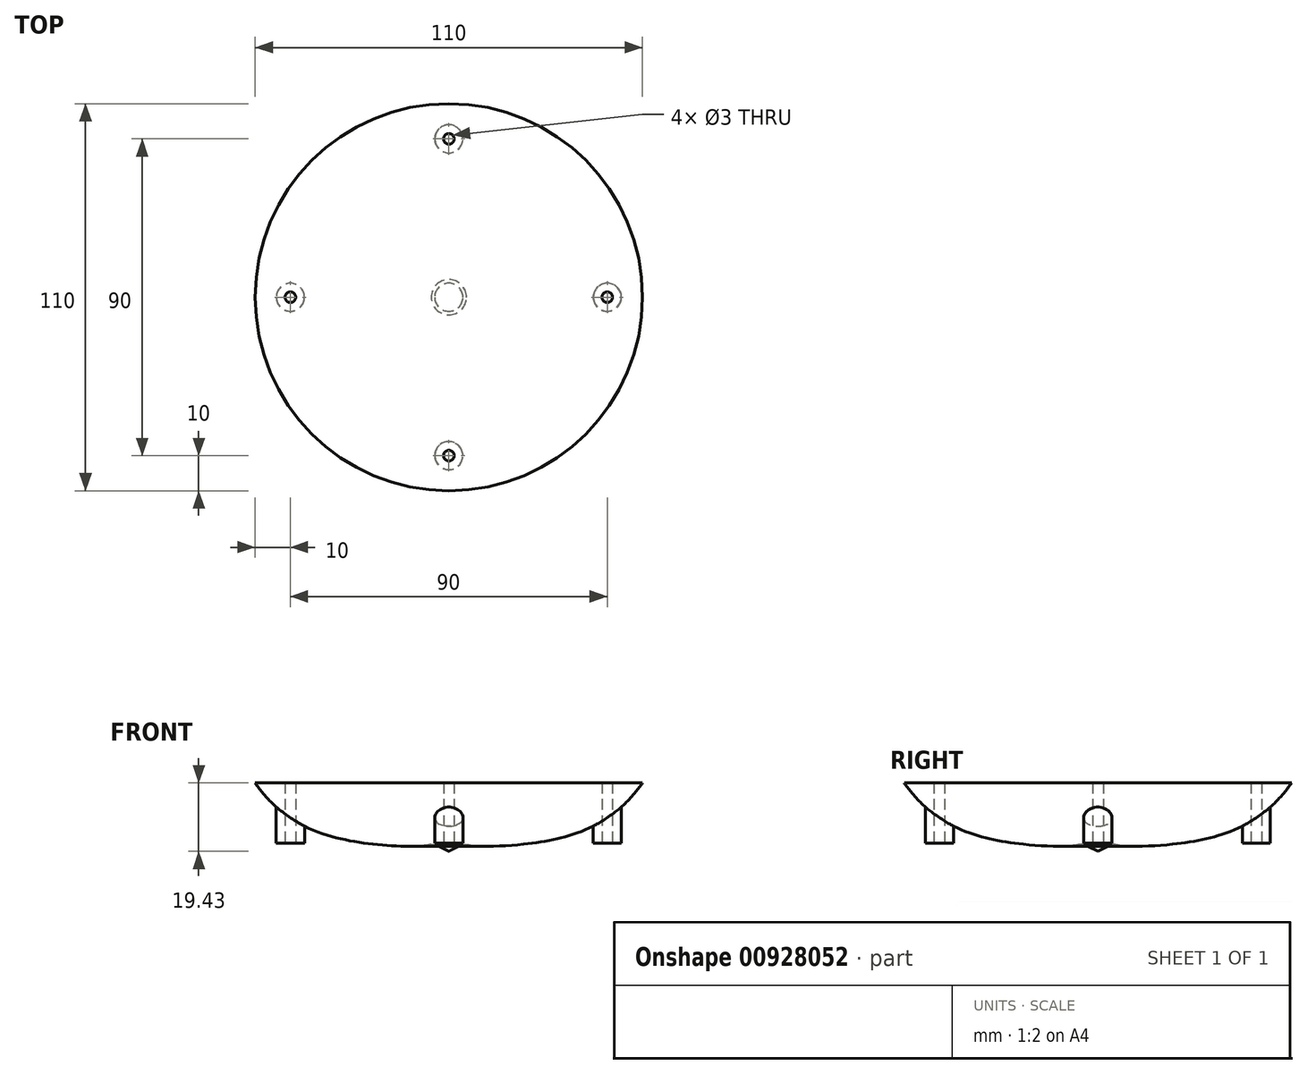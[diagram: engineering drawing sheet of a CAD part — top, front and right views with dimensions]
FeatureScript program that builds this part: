
annotation { "Feature Type Name" : "Feature", "Feature Type Description" : "" }
export const myFeature = defineFeature(function(context is Context, id is Id, definition is map)
    precondition{}
    {
        {
            var Q0;
            Q0=qCreatedBy(makeId("Front.planeOp"),FACE);
            var sketch = newSketch(context, id + "F0", { "sketchPlane" : qUnion([Q0])});
            skPoint(sketch, "E0", {"position": v(5, 2.5) * mm});
            skPoint(sketch, "E1", {"position": v(6, 2.28) * mm});
            skPoint(sketch, "E2", {"position": v(10, 1.95) * mm});
            skPoint(sketch, "E3", {"position": v(12, 1.95) * mm});
            skPoint(sketch, "E4", {"position": v(14, 2) * mm});
            skPoint(sketch, "E5", {"position": v(16, 2.1) * mm});
            skPoint(sketch, "E6", {"position": v(18, 2.22) * mm});
            skPoint(sketch, "E7", {"position": v(20, 2.4) * mm});
            skPoint(sketch, "E8", {"position": v(23, 2.72) * mm});
            skPoint(sketch, "E9", {"position": v(24, 2.85) * mm});
            skPoint(sketch, "E10", {"position": v(25, 3) * mm});
            skPoint(sketch, "E11", {"position": v(8, 2.04) * mm});
            skPoint(sketch, "E12", {"position": v(9, 1.98) * mm});
            skPoint(sketch, "E13", {"position": v(7, 2.13) * mm});
            skPoint(sketch, "E14", {"position": v(11, 1.94) * mm});
            skPoint(sketch, "E15", {"position": v(13, 1.97) * mm});
            skPoint(sketch, "E16", {"position": v(15, 2.04) * mm});
            skPoint(sketch, "E17", {"position": v(17, 2.15) * mm});
            skPoint(sketch, "E18", {"position": v(19, 2.3) * mm});
            skPoint(sketch, "E19", {"position": v(21, 2.5) * mm});
            skPoint(sketch, "E20", {"position": v(22, 2.6) * mm});
            skPoint(sketch, "E21", {"position": v(26, 3.15) * mm});
            skPoint(sketch, "E22", {"position": v(27, 3.31) * mm});
            skPoint(sketch, "E23", {"position": v(28, 3.5) * mm});
            skPoint(sketch, "E24", {"position": v(29, 3.7) * mm});
            skPoint(sketch, "E25", {"position": v(30, 3.9) * mm});
            skPoint(sketch, "E26", {"position": v(31, 4.13) * mm});
            skPoint(sketch, "E27", {"position": v(32, 4.37) * mm});
            skPoint(sketch, "E28", {"position": v(33, 4.64) * mm});
            skPoint(sketch, "E29", {"position": v(34, 4.92) * mm});
            skPoint(sketch, "E30", {"position": v(35, 5.23) * mm});
            skPoint(sketch, "E31", {"position": v(36, 5.56) * mm});
            skPoint(sketch, "E32", {"position": v(37, 5.92) * mm});
            skPoint(sketch, "E33", {"position": v(38, 6.3) * mm});
            skPoint(sketch, "E34", {"position": v(39, 6.71) * mm});
            skPoint(sketch, "E35", {"position": v(40, 7.16) * mm});
            skPoint(sketch, "E36", {"position": v(41, 7.64) * mm});
            skPoint(sketch, "E37", {"position": v(42, 8.15) * mm});
            skPoint(sketch, "E38", {"position": v(44, 9.31) * mm});
            skPoint(sketch, "E39", {"position": v(45, 9.95) * mm});
            skPoint(sketch, "E40", {"position": v(43, 8.71) * mm});
            skPoint(sketch, "E41", {"position": v(52, 16.11) * mm});
            skPoint(sketch, "E42", {"position": v(55, 19.93) * mm});
            skPoint(sketch, "E43", {"position": v(0, 0) * mm});
            skPoint(sketch, "E44", {"position": v(54, 18.56) * mm});
            skPoint(sketch, "E45", {"position": v(53, 17.29) * mm});
            skPoint(sketch, "E46", {"position": v(51, 15.02) * mm});
            skPoint(sketch, "E47", {"position": v(50, 14) * mm});
            skPoint(sketch, "E48", {"position": v(49, 13.07) * mm});
            skPoint(sketch, "E49", {"position": v(48, 12.2) * mm});
            skPoint(sketch, "E50", {"position": v(47, 11.4) * mm});
            skPoint(sketch, "E51", {"position": v(46, 10.65) * mm});
            skPoint(sketch, "E52", {"position": v(0, 2.5) * mm});
            skLineSegment(sketch, "E53", {"start": v(0, 2.5) * mm, "end": v(5, 2.5) * mm});
            skFitSpline(sketch, "E54", {"points": [v(5, 2.5) * mm, v(6, 2.28) * mm, v(7, 2.13) * mm, v(8, 2.04) * mm, v(9, 1.98) * mm, v(10, 1.95) * mm, v(11, 1.94) * mm, v(12, 1.95) * mm, v(13, 1.97) * mm, v(14, 2) * mm, v(15, 2.04) * mm, v(16, 2.1) * mm, v(17, 2.15) * mm, v(18, 2.22) * mm, v(19, 2.3) * mm, v(20, 2.4) * mm, v(21, 2.5) * mm, v(22, 2.6) * mm, v(23, 2.72) * mm, v(24, 2.85) * mm, v(25, 3) * mm, v(26, 3.15) * mm, v(27, 3.31) * mm, v(28, 3.5) * mm, v(29, 3.7) * mm, v(30, 3.9) * mm, v(31, 4.13) * mm, v(32, 4.37) * mm, v(33, 4.64) * mm, v(34, 4.92) * mm, v(35, 5.23) * mm, v(36, 5.56) * mm, v(37, 5.92) * mm, v(38, 6.3) * mm, v(39, 6.71) * mm, v(40, 7.16) * mm, v(41, 7.64) * mm, v(42, 8.15) * mm, v(43, 8.71) * mm, v(44, 9.31) * mm, v(45, 9.95) * mm, v(46, 10.65) * mm, v(47, 11.4) * mm, v(48, 12.2) * mm, v(49, 13.07) * mm, v(50, 14) * mm, v(51, 15.02) * mm, v(52, 16.11) * mm, v(53, 17.29) * mm, v(54, 18.56) * mm, v(55, 19.93) * mm], "startDerivative": vector(51.92, -12.2) * mm, "endDerivative": vector(40.18, 55.95) * mm});
            skPoint(sketch, "E55", {"position": v(0, 19.93) * mm});
            skLineSegment(sketch, "E56", {"start": v(0, 2.5) * mm, "end": v(0, 19.93) * mm});
            skLineSegment(sketch, "E57", {"start": v(0, 19.93) * mm, "end": v(55, 19.93) * mm});
            skLineSegment(sketch, "E58", {"start": v(0, -53.88) * mm, "end": v(0, 63.92) * mm, "construction": true});
            skSolve(sketch);
        }
        {
            var Q0;
            Q0=makeQuery(id+"F0.imprint","IMPRINT",FACE,{"disambiguationData":[TD([[makeQuery(id+"F0.imprint","IMPRINT",EDGE,{"derivedFrom":sQuery(id+"F0.wireOp",EDGE,"E53")}),1.0]])]});
            var Q1;
            Q1=sQuery(id+"F0.wireOp",EDGE,"E58");
            revolve(context, id + "F1", {"surfaceOperationType" : NewSurfaceOperationType.NEW, "entities" : qUnion([Q0]), "axis" : qUnion([Q1]), "revolveType" : RevolveType.FULL});
        }
        {
            var Q0;
            Q0=qCreatedBy(makeId("Top.planeOp"),FACE);
            cPlane(context, id + "F2", {"entities" : qUnion([Q0]), "cplaneType" : CPlaneType.OFFSET, "offset" : 2.8 * mm, "width" : 150 * mm, "height" : 150 * mm});
        }
        {
            var Q0;
            Q0=qCreatedBy(id+"F2.planeOp",FACE);
            var sketch = newSketch(context, id + "F3", { "sketchPlane" : qUnion([Q0])});
            skCircle(sketch, "E59", {"center": v(45, 0) * mm, "radius": 4 * mm});
            skCircle(sketch, "E60.1.1", {"center": v(0, 45) * mm, "radius": 4 * mm});
            skCircle(sketch, "E60.2.1", {"center": v(-45, 0) * mm, "radius": 4 * mm});
            skCircle(sketch, "E60.3.1", {"center": v(0, -45) * mm, "radius": 4 * mm});
            skPoint(sketch, "E60.center", {"position": v(0, 0) * mm});
            skSolve(sketch);
        }
        {
            var Q0;
            Q0=makeQuery(id+"F3.imprint","IMPRINT",FACE,{"disambiguationData":[TD([[makeQuery(id+"F3.imprint","IMPRINT",EDGE,{"derivedFrom":sQuery(id+"F3.wireOp",EDGE,"E60.3.1")}),1.0]])]});
            var Q1;
            Q1=makeQuery(id+"F3.imprint","IMPRINT",FACE,{"disambiguationData":[TD([[makeQuery(id+"F3.imprint","IMPRINT",EDGE,{"derivedFrom":sQuery(id+"F3.wireOp",EDGE,"E59")}),1.0]])]});
            var Q2;
            Q2=makeQuery(id+"F3.imprint","IMPRINT",FACE,{"disambiguationData":[TD([[makeQuery(id+"F3.imprint","IMPRINT",EDGE,{"derivedFrom":sQuery(id+"F3.wireOp",EDGE,"E60.1.1")}),1.0]])]});
            var Q3;
            Q3=makeQuery(id+"F3.imprint","IMPRINT",FACE,{"disambiguationData":[TD([[makeQuery(id+"F3.imprint","IMPRINT",EDGE,{"derivedFrom":sQuery(id+"F3.wireOp",EDGE,"E60.2.1")}),1.0]])]});
            extrude(context, id + "F4", {"entities" : qUnion([Q0, Q1, Q2, Q3]), "operationType" : NewBodyOperationType.ADD, "depth" : 12 * mm, "offsetDistance" : 25 * mm});
        }
        {
            var Q0;
            Q0=qCreatedBy(id+"F2.planeOp",FACE);
            var sketch = newSketch(context, id + "F5", { "sketchPlane" : qUnion([Q0])});
            skCircle(sketch, "E61", {"center": v(45, 0) * mm, "radius": 1.5 * mm});
            skCircle(sketch, "E62.1.0", {"center": v(0, 45) * mm, "radius": 1.5 * mm});
            skCircle(sketch, "E62.2.0", {"center": v(-45, 0) * mm, "radius": 1.5 * mm});
            skCircle(sketch, "E62.3.0", {"center": v(0, -45) * mm, "radius": 1.5 * mm});
            skPoint(sketch, "E62.center", {"position": v(0, 0) * mm});
            skSolve(sketch);
        }
        {
            var Q0;
            Q0=makeQuery(id+"F5.imprint","IMPRINT",FACE,{"disambiguationData":[TD([[makeQuery(id+"F5.imprint","IMPRINT",EDGE,{"derivedFrom":sQuery(id+"F5.wireOp",EDGE,"E61")}),1.0]])]});
            var Q1;
            Q1=makeQuery(id+"F5.imprint","IMPRINT",FACE,{"disambiguationData":[TD([[makeQuery(id+"F5.imprint","IMPRINT",EDGE,{"derivedFrom":sQuery(id+"F5.wireOp",EDGE,"E62.3.0")}),1.0]])]});
            var Q2;
            Q2=makeQuery(id+"F5.imprint","IMPRINT",FACE,{"disambiguationData":[TD([[makeQuery(id+"F5.imprint","IMPRINT",EDGE,{"derivedFrom":sQuery(id+"F5.wireOp",EDGE,"E62.2.0")}),1.0]])]});
            var Q3;
            Q3=makeQuery(id+"F5.imprint","IMPRINT",FACE,{"disambiguationData":[TD([[makeQuery(id+"F5.imprint","IMPRINT",EDGE,{"derivedFrom":sQuery(id+"F5.wireOp",EDGE,"E62.1.0")}),1.0]])]});
            extrude(context, id + "F6", {"entities" : qUnion([Q0, Q1, Q2, Q3]), "operationType" : NewBodyOperationType.REMOVE, "depth" : 25 * mm, "offsetDistance" : 25 * mm});
        }
        {
            var Q0;
            Q0=qCreatedBy(makeId("Front.planeOp"),FACE);
            var sketch = newSketch(context, id + "F7", { "sketchPlane" : qUnion([Q0])});
            skLineSegment(sketch, "E63", {"start": v(0, 2.5) * mm, "end": v(4, 2.5) * mm});
            skLineSegment(sketch, "E64", {"start": v(4, 2.5) * mm, "end": v(0, 0.5) * mm});
            skLineSegment(sketch, "E65", {"start": v(0, 0.5) * mm, "end": v(0, 2.5) * mm});
            skLineSegment(sketch, "E66", {"start": v(0, -24.06) * mm, "end": v(0, 44) * mm, "construction": true});
            skSolve(sketch);
        }
        {
            var Q0;
            Q0=makeQuery(id+"F7.imprint","IMPRINT",FACE,{"disambiguationData":[TD([[makeQuery(id+"F7.imprint","IMPRINT",EDGE,{"derivedFrom":sQuery(id+"F7.wireOp",EDGE,"E63")}),-1.0]])]});
            var Q1;
            Q1=sQuery(id+"F7.wireOp",EDGE,"E66");
            revolve(context, id + "F8", {"surfaceOperationType" : NewSurfaceOperationType.NEW, "entities" : qUnion([Q0]), "axis" : qUnion([Q1]), "revolveType" : RevolveType.FULL});
        }
    });
